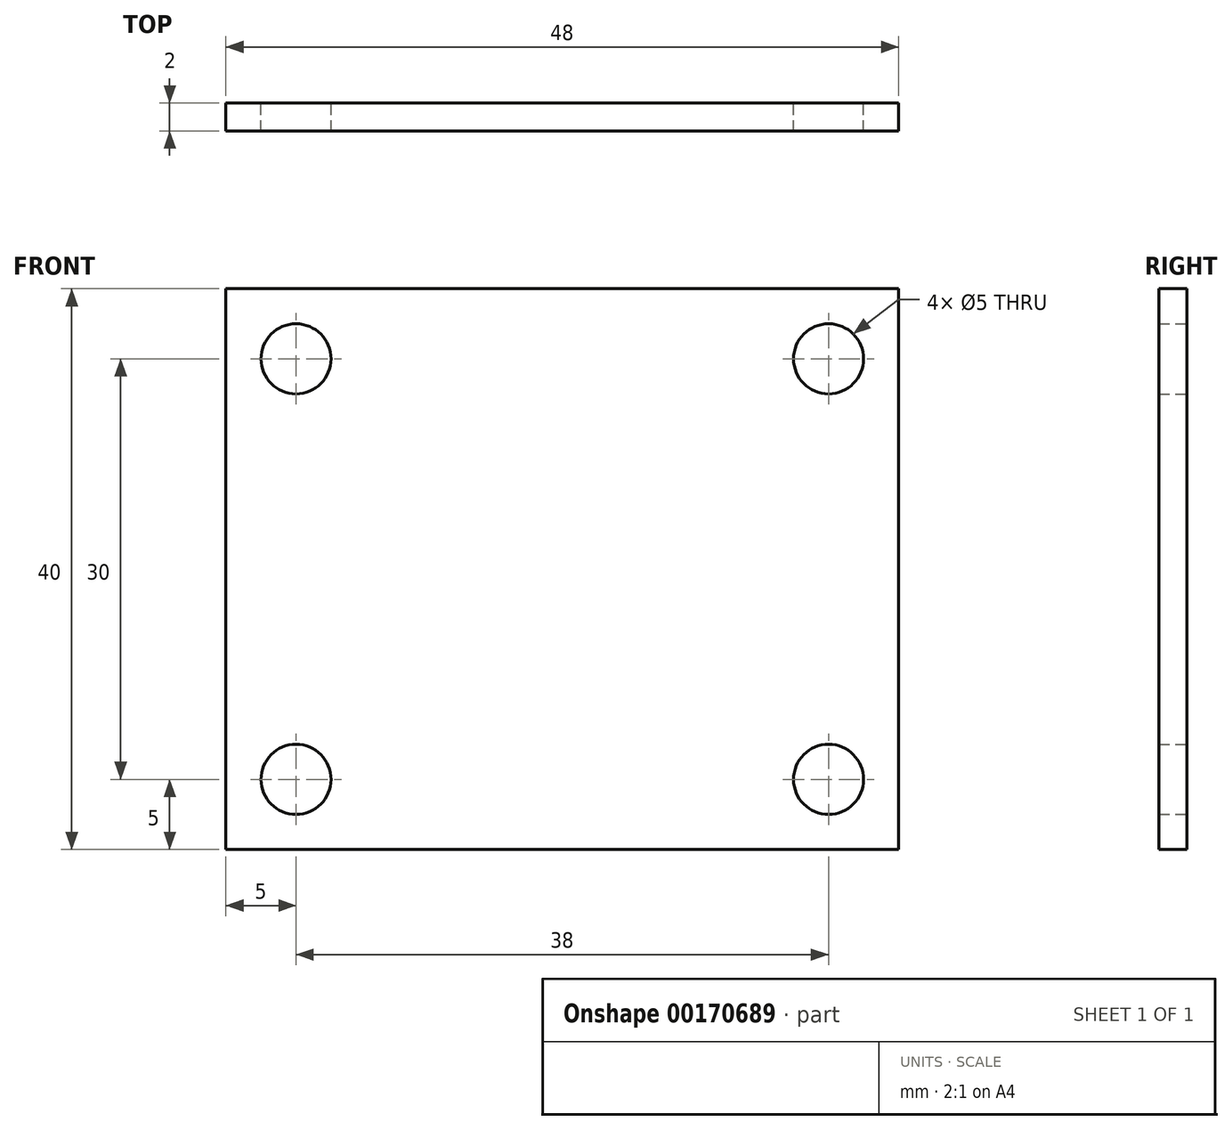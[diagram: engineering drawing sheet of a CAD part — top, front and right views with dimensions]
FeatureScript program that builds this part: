
annotation { "Feature Type Name" : "Feature", "Feature Type Description" : "" }
export const myFeature = defineFeature(function(context is Context, id is Id, definition is map)
    precondition{}
    {
        {
            var Q0;
            Q0=qCreatedBy(makeId("Front.planeOp"),FACE);
            var sketch = newSketch(context, id + "F0", { "sketchPlane" : qUnion([Q0])});
            skLineSegment(sketch, "E0.bottom", {"start": v(19, 15) * mm, "end": v(-19, 15) * mm, "construction": true});
            skLineSegment(sketch, "E0.top", {"start": v(19, -15) * mm, "end": v(-19, -15) * mm, "construction": true});
            skLineSegment(sketch, "E0.left", {"start": v(19, 15) * mm, "end": v(19, -15) * mm, "construction": true});
            skLineSegment(sketch, "E0.right", {"start": v(-19, 15) * mm, "end": v(-19, -15) * mm, "construction": true});
            skLineSegment(sketch, "E1.0", {"start": v(-24, 20) * mm, "end": v(-24, -20) * mm});
            skLineSegment(sketch, "E1.1", {"start": v(24, 20) * mm, "end": v(-24, 20) * mm});
            skLineSegment(sketch, "E1.2", {"start": v(24, 20) * mm, "end": v(24, -20) * mm});
            skLineSegment(sketch, "E1.3", {"start": v(24, -20) * mm, "end": v(-24, -20) * mm});
            skCircle(sketch, "E2", {"center": v(-19, 15) * mm, "radius": 2.5 * mm});
            skCircle(sketch, "E3", {"center": v(19, 15) * mm, "radius": 2.5 * mm});
            skCircle(sketch, "E4", {"center": v(19, -15) * mm, "radius": 2.5 * mm});
            skCircle(sketch, "E5", {"center": v(-19, -15) * mm, "radius": 2.5 * mm});
            skSolve(sketch);
        }
        {
            var Q0;
            Q0=makeQuery(id+"F0.imprint","IMPRINT",FACE,{"disambiguationData":[TD([[makeQuery(id+"F0.imprint","IMPRINT",EDGE,{"derivedFrom":sQuery(id+"F0.wireOp",EDGE,"E1.0")}),1.0]])]});
            extrude(context, id + "F1", {"entities" : qUnion([Q0]), "depth" : 2 * mm});
        }
    });
